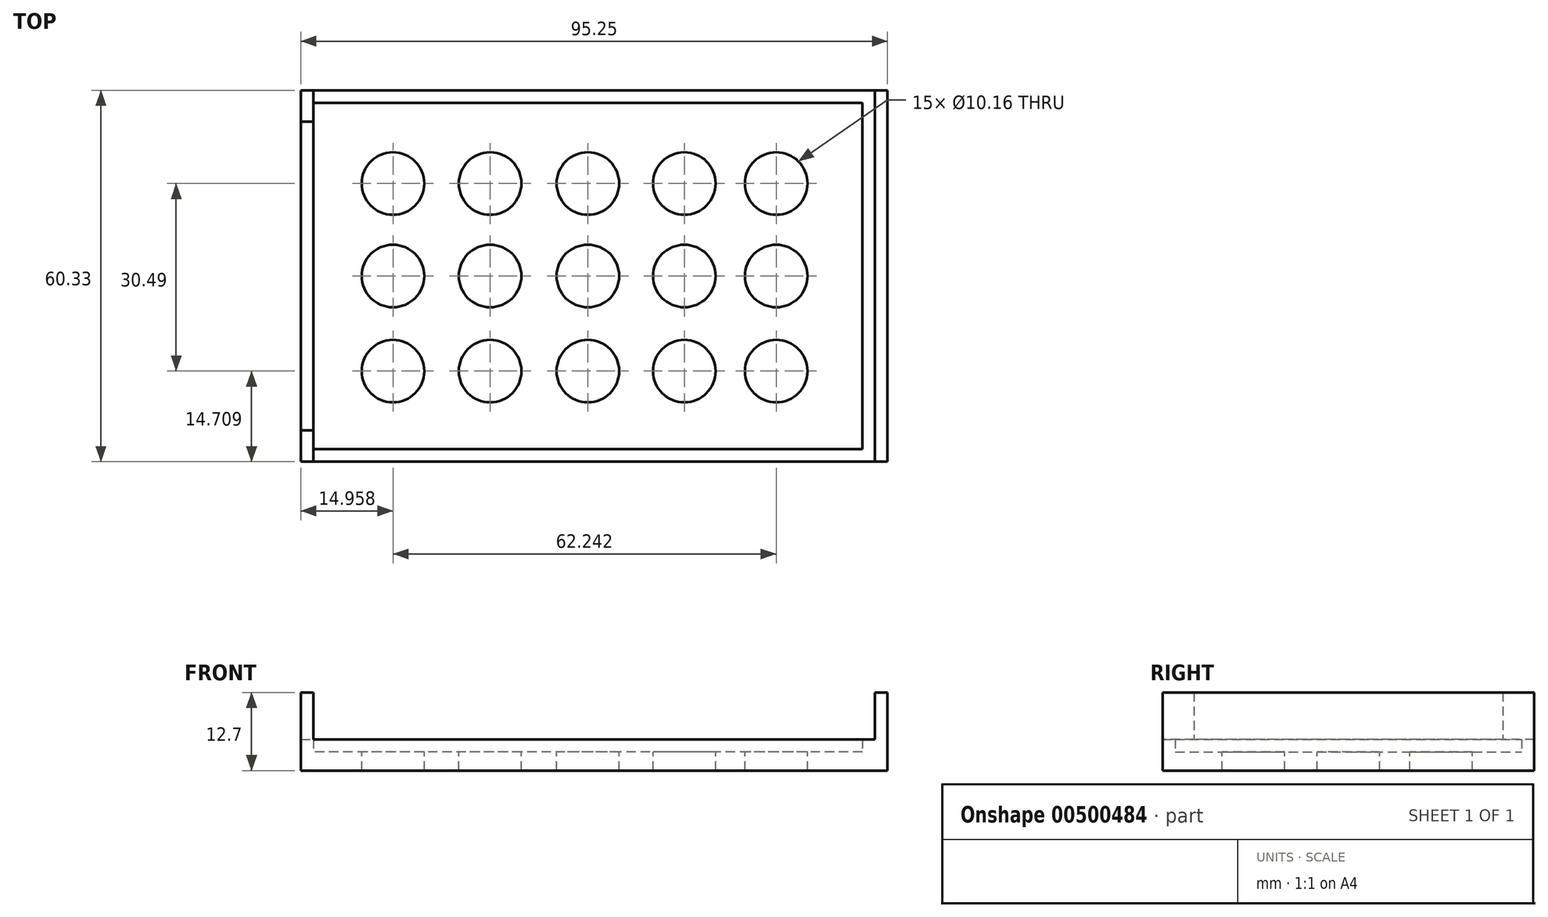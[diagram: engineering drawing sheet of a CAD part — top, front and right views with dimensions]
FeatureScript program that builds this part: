
annotation { "Feature Type Name" : "Feature", "Feature Type Description" : "" }
export const myFeature = defineFeature(function(context is Context, id is Id, definition is map)
    precondition{}
    {
        {
            var Q0;
            Q0=qCreatedBy(makeId("Top.planeOp"),FACE);
            var sketch = newSketch(context, id + "F0", { "sketchPlane" : qUnion([Q0])});
            skLineSegment(sketch, "E0.bottom", {"start": v(-54.5, 12.08) * mm, "end": v(40.76, 12.08) * mm});
            skLineSegment(sketch, "E0.top", {"start": v(-54.5, -48.25) * mm, "end": v(40.76, -48.25) * mm});
            skLineSegment(sketch, "E0.left", {"start": v(-54.5, 12.08) * mm, "end": v(-54.5, -48.25) * mm});
            skLineSegment(sketch, "E0.right", {"start": v(40.76, 12.08) * mm, "end": v(40.76, -48.25) * mm});
            skSolve(sketch);
        }
        {
            var Q0;
            Q0 = qSketchRegion(id + "F0", true);
            extrude(context, id + "F1", {"entities" : qUnion([Q0]), "depth" : 3.05 * mm});
        }
        {
            var Q0;
            Q0=makeQuery(id+"F1.opExtrude","CAP_FACE",FACE,{"disambiguationData":[OSD([sQuery(id+"F0.wireOp",EDGE,"E0.bottom"),sQuery(id+"F0.wireOp",EDGE,"E0.top"),sQuery(id+"F0.wireOp",EDGE,"E0.left"),sQuery(id+"F0.wireOp",EDGE,"E0.right")])],"isStart":false});
            var sketch = newSketch(context, id + "F2", { "sketchPlane" : qUnion([Q0])});
            skLineSegment(sketch, "E1", {"start": v(40.76, 12.08) * mm, "end": v(38.72, 12.08) * mm});
            skLineSegment(sketch, "E2", {"start": v(38.72, 12.08) * mm, "end": v(38.72, -48.25) * mm});
            skLineSegment(sketch, "E3", {"start": v(38.72, -48.25) * mm, "end": v(40.76, -48.25) * mm});
            skLineSegment(sketch, "E4", {"start": v(40.76, -48.25) * mm, "end": v(40.76, 12.08) * mm});
            skSolve(sketch);
        }
        {
            var Q0;
            Q0 = qSketchRegion(id + "F2", true);
            extrude(context, id + "F3", {"entities" : qUnion([Q0]), "operationType" : NewBodyOperationType.ADD, "depth" : 9.65 * mm});
        }
        {
            var Q0;
            Q0=makeQuery(id+"F1.opExtrude","CAP_FACE",FACE,{"disambiguationData":[OSD([sQuery(id+"F0.wireOp",EDGE,"E0.bottom"),sQuery(id+"F0.wireOp",EDGE,"E0.top"),sQuery(id+"F0.wireOp",EDGE,"E0.left"),sQuery(id+"F0.wireOp",EDGE,"E0.right")])],"isStart":false});
            var sketch = newSketch(context, id + "F4", { "sketchPlane" : qUnion([Q0])});
            skLineSegment(sketch, "E5.bottom", {"start": v(-54.5, -48.25) * mm, "end": v(-52.46, -48.25) * mm});
            skLineSegment(sketch, "E5.top", {"start": v(-54.5, -43.17) * mm, "end": v(-52.46, -43.17) * mm});
            skLineSegment(sketch, "E5.left", {"start": v(-54.5, -48.25) * mm, "end": v(-54.5, -43.17) * mm});
            skLineSegment(sketch, "E5.right", {"start": v(-52.46, -48.25) * mm, "end": v(-52.46, -43.17) * mm});
            skSolve(sketch);
        }
        {
            var Q0;
            Q0 = qSketchRegion(id + "F4", true);
            extrude(context, id + "F5", {"entities" : qUnion([Q0]), "operationType" : NewBodyOperationType.ADD, "depth" : 9.65 * mm});
        }
        {
            var Q0;
            Q0=makeQuery(id+"F1.opExtrude","CAP_FACE",FACE,{"disambiguationData":[OSD([sQuery(id+"F0.wireOp",EDGE,"E0.bottom"),sQuery(id+"F0.wireOp",EDGE,"E0.top"),sQuery(id+"F0.wireOp",EDGE,"E0.left"),sQuery(id+"F0.wireOp",EDGE,"E0.right")])],"isStart":false});
            var sketch = newSketch(context, id + "F6", { "sketchPlane" : qUnion([Q0])});
            skLineSegment(sketch, "E6.bottom", {"start": v(-54.5, 12.08) * mm, "end": v(-52.46, 12.08) * mm});
            skLineSegment(sketch, "E6.top", {"start": v(-54.5, 7) * mm, "end": v(-52.46, 7) * mm});
            skLineSegment(sketch, "E6.left", {"start": v(-54.5, 12.08) * mm, "end": v(-54.5, 7) * mm});
            skLineSegment(sketch, "E6.right", {"start": v(-52.46, 12.08) * mm, "end": v(-52.46, 7) * mm});
            skSolve(sketch);
        }
        {
            var Q0;
            Q0 = qSketchRegion(id + "F6", true);
            extrude(context, id + "F7", {"entities" : qUnion([Q0]), "operationType" : NewBodyOperationType.ADD, "depth" : 9.65 * mm});
        }
        {
            var Q0;
            Q0=makeQuery(id+"F1.opExtrude","CAP_FACE",FACE,{"disambiguationData":[OSD([sQuery(id+"F0.wireOp",EDGE,"E0.bottom"),sQuery(id+"F0.wireOp",EDGE,"E0.top"),sQuery(id+"F0.wireOp",EDGE,"E0.left"),sQuery(id+"F0.wireOp",EDGE,"E0.right")])],"isStart":false});
            var sketch = newSketch(context, id + "F8", { "sketchPlane" : qUnion([Q0])});
            skLineSegment(sketch, "E7", {"start": v(-52.46, 12.08) * mm, "end": v(38.72, 12.08) * mm});
            skLineSegment(sketch, "E8", {"start": v(38.72, 12.08) * mm, "end": v(38.72, 10.05) * mm});
            skLineSegment(sketch, "E9", {"start": v(38.72, 10.05) * mm, "end": v(-52.46, 10.05) * mm});
            skLineSegment(sketch, "E10", {"start": v(-52.46, 10.05) * mm, "end": v(-52.46, 12.08) * mm});
            skLineSegment(sketch, "E11", {"start": v(-52.46, -48.25) * mm, "end": v(38.72, -48.25) * mm});
            skLineSegment(sketch, "E12", {"start": v(38.72, -48.25) * mm, "end": v(38.72, -46.22) * mm});
            skLineSegment(sketch, "E13", {"start": v(38.72, -46.22) * mm, "end": v(-52.46, -46.22) * mm});
            skLineSegment(sketch, "E14", {"start": v(-52.46, -46.22) * mm, "end": v(-52.46, -48.25) * mm});
            skSolve(sketch);
        }
        {
            var Q0;
            Q0 = qSketchRegion(id + "F8", true);
            extrude(context, id + "F9", {"entities" : qUnion([Q0]), "operationType" : NewBodyOperationType.ADD, "depth" : 2.03 * mm});
        }
        {
            var Q0;
            Q0=makeQuery(id+"F1.opExtrude","CAP_FACE",FACE,{"disambiguationData":[OSD([sQuery(id+"F0.wireOp",EDGE,"E0.bottom"),sQuery(id+"F0.wireOp",EDGE,"E0.top"),sQuery(id+"F0.wireOp",EDGE,"E0.left"),sQuery(id+"F0.wireOp",EDGE,"E0.right")])],"isStart":false});
            var sketch = newSketch(context, id + "F10", { "sketchPlane" : qUnion([Q0])});
            skLineSegment(sketch, "E15", {"start": v(-52.46, 7) * mm, "end": v(-54.5, 7) * mm});
            skLineSegment(sketch, "E16", {"start": v(-54.5, 7) * mm, "end": v(-54.5, -43.17) * mm});
            skLineSegment(sketch, "E17", {"start": v(-54.5, -43.17) * mm, "end": v(-52.46, -43.17) * mm});
            skLineSegment(sketch, "E18", {"start": v(-52.46, -43.17) * mm, "end": v(-52.46, 7) * mm});
            skSolve(sketch);
        }
        {
            var Q0;
            Q0 = qSketchRegion(id + "F10", true);
            extrude(context, id + "F11", {"entities" : qUnion([Q0]), "operationType" : NewBodyOperationType.ADD, "depth" : 2.03 * mm});
        }
        {
            var Q0;
            Q0=makeQuery(id+"F1.opExtrude","CAP_FACE",FACE,{"disambiguationData":[OSD([sQuery(id+"F0.wireOp",EDGE,"E0.bottom"),sQuery(id+"F0.wireOp",EDGE,"E0.top"),sQuery(id+"F0.wireOp",EDGE,"E0.left"),sQuery(id+"F0.wireOp",EDGE,"E0.right")])],"isStart":false});
            var sketch = newSketch(context, id + "F12", { "sketchPlane" : qUnion([Q0])});
            skLineSegment(sketch, "E19", {"start": v(38.72, -46.22) * mm, "end": v(36.7, -46.22) * mm});
            skLineSegment(sketch, "E20", {"start": v(36.7, -46.22) * mm, "end": v(36.7, 10.05) * mm});
            skLineSegment(sketch, "E21", {"start": v(36.7, 10.05) * mm, "end": v(38.72, 10.05) * mm});
            skLineSegment(sketch, "E22", {"start": v(38.72, 10.05) * mm, "end": v(38.72, -46.22) * mm});
            skSolve(sketch);
        }
        {
            var Q0;
            Q0 = qSketchRegion(id + "F12", true);
            extrude(context, id + "F13", {"entities" : qUnion([Q0]), "operationType" : NewBodyOperationType.ADD, "depth" : 2.03 * mm});
        }
        {
            var Q0;
            Q0=makeQuery(id+"F1.opExtrude","CAP_FACE",FACE,{"disambiguationData":[OSD([sQuery(id+"F0.wireOp",EDGE,"E0.bottom"),sQuery(id+"F0.wireOp",EDGE,"E0.top"),sQuery(id+"F0.wireOp",EDGE,"E0.left"),sQuery(id+"F0.wireOp",EDGE,"E0.right")])],"isStart":false});
            var sketch = newSketch(context, id + "F14", { "sketchPlane" : qUnion([Q0])});
            skCircle(sketch, "E23", {"center": v(-39.53, -3.05) * mm, "radius": 5.08 * mm});
            skCircle(sketch, "E24", {"center": v(-23.76, -3.05) * mm, "radius": 5.08 * mm});
            skCircle(sketch, "E25", {"center": v(-7.89, -3.05) * mm, "radius": 5.08 * mm});
            skCircle(sketch, "E26", {"center": v(7.78, -3.05) * mm, "radius": 5.08 * mm});
            skCircle(sketch, "E27", {"center": v(22.7, -3.05) * mm, "radius": 5.08 * mm});
            skCircle(sketch, "E28", {"center": v(22.7, -18.08) * mm, "radius": 5.08 * mm});
            skCircle(sketch, "E29", {"center": v(7.78, -18.08) * mm, "radius": 5.08 * mm});
            skCircle(sketch, "E30", {"center": v(-7.89, -18.08) * mm, "radius": 5.08 * mm});
            skCircle(sketch, "E31", {"center": v(-23.76, -18.08) * mm, "radius": 5.08 * mm});
            skCircle(sketch, "E32", {"center": v(-39.53, -18.08) * mm, "radius": 5.08 * mm});
            skCircle(sketch, "E33", {"center": v(-39.53, -33.54) * mm, "radius": 5.08 * mm});
            skCircle(sketch, "E34", {"center": v(-23.76, -33.54) * mm, "radius": 5.08 * mm});
            skCircle(sketch, "E35", {"center": v(-7.89, -33.54) * mm, "radius": 5.08 * mm});
            skCircle(sketch, "E36", {"center": v(22.7, -33.54) * mm, "radius": 5.08 * mm});
            skCircle(sketch, "E37", {"center": v(7.78, -33.54) * mm, "radius": 5.08 * mm});
            skSolve(sketch);
        }
        {
            var Q0;
            Q0 = qSketchRegion(id + "F14", true);
            extrude(context, id + "F15", {"entities" : qUnion([Q0]), "operationType" : NewBodyOperationType.REMOVE, "oppositeDirection" : true, "depth" : 25.4 * mm});
        }
    });
